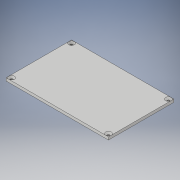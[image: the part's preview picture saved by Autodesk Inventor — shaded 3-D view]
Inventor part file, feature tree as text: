
AUTODESK INVENTOR PART (.ipt)
format: ipt  version: 2019.4 (Build 234330000, 330)  size: 113,664 bytes
history: native  units: mm
features: sketch x2, extrude x1, hole x1, pattern_linear x1
ambient origin geometry x8: Origin, YZ Plane, XZ Plane, XY Plane, X Axis, Y Axis, Z Axis, Center Point
bodies: Solid1 (feature_tree)
feature tree (5):
  extrude  "Extrusion1"  Depth=73.5mm
  hole  "Hole1"  [1 undecoded]
  pattern_linear  "Rectangular Pattern1"  Spacing1=2.0mm  [1 undecoded]
  sketch  "Sketch1"  dims[d0=47.0mm d1=73.5mm]
  sketch  "Sketch2"  dims[d2=2.0mm d3=0.0mm d4=2.0mm d5=2.0mm d6=1.694mm d7=2.0mm d8=4.0mm d9=2.0mm d10=90.0deg d11=2.0mm d12=0.0mm d13=20.0mm d15=43.0mm d16=20.0mm d18=69.5mm]
note: 2 required parameter values undecoded (feature->parameter linkage not recoverable at this tier; creation-order binding heuristic only, values carry confidence <= 0.55)
